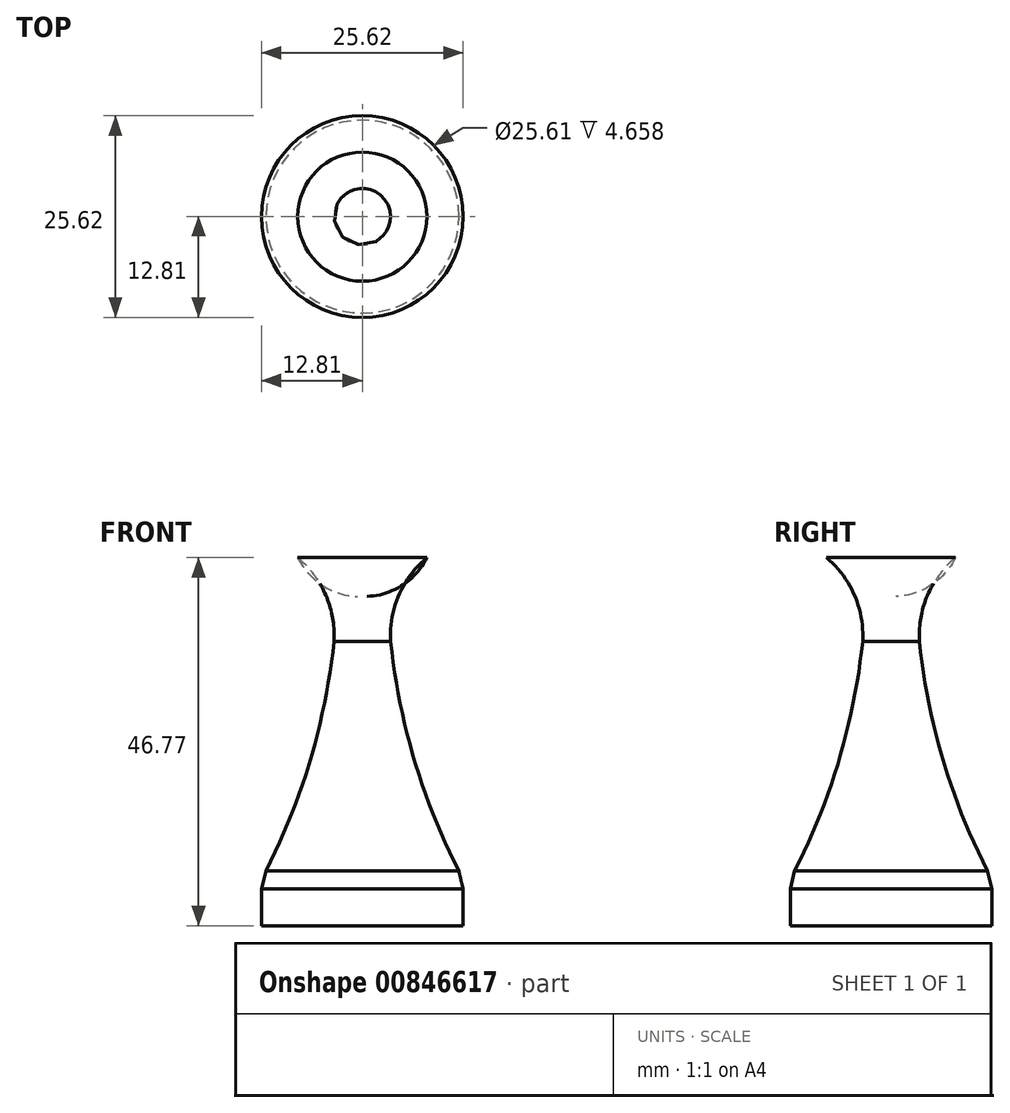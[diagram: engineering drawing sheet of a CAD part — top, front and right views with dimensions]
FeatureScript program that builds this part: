
annotation { "Feature Type Name" : "Feature", "Feature Type Description" : "" }
export const myFeature = defineFeature(function(context is Context, id is Id, definition is map)
    precondition{}
    {
        {
            var Q0;
            Q0=qCreatedBy(makeId("Front.planeOp"),FACE);
            var sketch = newSketch(context, id + "F0", { "sketchPlane" : qUnion([Q0])});
            skLineSegment(sketch, "E0", {"start": v(0, 0) * mm, "end": v(0, 59.43) * mm, "construction": true});
            skArc(sketch, "E1", {"start": v(0, 59.43) * mm, "mid": v(-7.68, 55.42) * mm, "end": v(-8.2, 46.77) * mm});
            skArc(sketch, "E2", {"start": v(-3.6, 36.12) * mm, "mid": v(-4.64, 41.99) * mm, "end": v(-8.2, 46.77) * mm});
            skArc(sketch, "E3", {"start": v(-12.8, 5.9) * mm, "mid": v(-6.75, 20.57) * mm, "end": v(-3.6, 36.12) * mm});
            skLineSegment(sketch, "E4", {"start": v(-12.8, 5.9) * mm, "end": v(-12.8, 0) * mm});
            skLineSegment(sketch, "E5", {"start": v(-12.8, 0) * mm, "end": v(0, 0) * mm});
            skLineSegment(sketch, "E6", {"start": v(0, 59.43) * mm, "end": v(0, 0) * mm});
            skSolve(sketch);
        }
        {
            var Q0;
            Q0=makeQuery(id+"F0.imprint","IMPRINT",FACE,{"disambiguationData":[TD([[makeQuery(id+"F0.imprint","IMPRINT",EDGE,{"derivedFrom":sQuery(id+"F0.wireOp",EDGE,"E1")}),1.0]])]});
            var Q1;
            Q1=sQuery(id+"F0.wireOp",EDGE,"E6");
            revolve(context, id + "F1", {"surfaceOperationType" : NewSurfaceOperationType.NEW, "entities" : qUnion([Q0]), "axis" : qUnion([Q1]), "revolveType" : RevolveType.FULL});
        }
        {
            var Q0;
            Q0=makeQuery(id+"F1.opRevolve","SWEPT_EDGE",EDGE,{"disambiguationData":[OSD([sQuery(id+"F0.wireOp",EDGE,"E3"),sQuery(id+"F0.wireOp",EDGE,"E4")])]});
            chamfer(context, id + "F2", {"entities" : qUnion([Q0]), "width" : 5.08 * mm, "tangentPropagation" : true});
        }
    });
